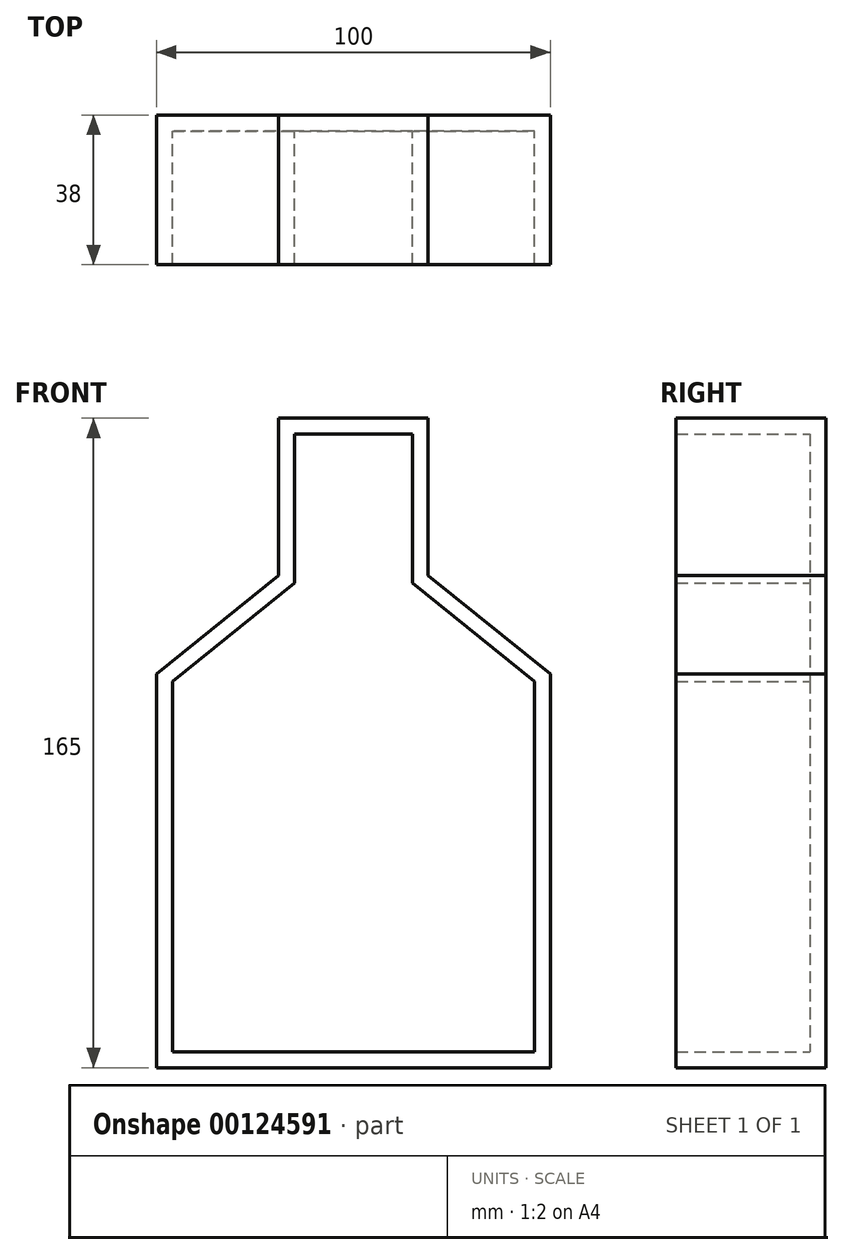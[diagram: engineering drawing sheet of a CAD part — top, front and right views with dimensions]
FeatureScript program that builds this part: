
annotation { "Feature Type Name" : "Feature", "Feature Type Description" : "" }
export const myFeature = defineFeature(function(context is Context, id is Id, definition is map)
    precondition{}
    {
        {
            var Q0;
            Q0=qCreatedBy(makeId("Front.planeOp"),FACE);
            var sketch = newSketch(context, id + "F0", { "sketchPlane" : qUnion([Q0])});
            skLineSegment(sketch, "E0", {"start": v(-50, -75) * mm, "end": v(50, -75) * mm});
            skLineSegment(sketch, "E1", {"start": v(50, -75) * mm, "end": v(50, 25) * mm});
            skLineSegment(sketch, "E2", {"start": v(19, 90) * mm, "end": v(-19, 90) * mm});
            skLineSegment(sketch, "E3", {"start": v(-50, 25) * mm, "end": v(-50, -75) * mm});
            skLineSegment(sketch, "E4", {"start": v(-19, 90) * mm, "end": v(-19, 50) * mm});
            skLineSegment(sketch, "E5", {"start": v(-19, 50) * mm, "end": v(-50, 25) * mm});
            skLineSegment(sketch, "E6", {"start": v(19, 90) * mm, "end": v(19, 50) * mm});
            skLineSegment(sketch, "E7", {"start": v(50, 25) * mm, "end": v(19, 50) * mm});
            skSolve(sketch);
        }
        {
            var Q0;
            Q0 = qSketchRegion(id + "F0", true);
            extrude(context, id + "F1", {"entities" : qUnion([Q0]), "endBound" : BoundingType.SYMMETRIC, "depth" : 38 * mm});
        }
        {
            var Q0;
            Q0=makeQuery(id+"F1.opExtrude","CAP_FACE",FACE,{"disambiguationData":[OSD([sQuery(id+"F0.wireOp",EDGE,"E0"),sQuery(id+"F0.wireOp",EDGE,"E1"),sQuery(id+"F0.wireOp",EDGE,"wSn0D2Qj-3Zax-uCmw-o4nf-oXh15RCH9NpI"),sQuery(id+"F0.wireOp",EDGE,"lb0Cxtu6-hfBw-rpJw-cRh2-uOisXKPZe3ND"),sQuery(id+"F0.wireOp",EDGE,"E2"),sQuery(id+"F0.wireOp",EDGE,"AijqVBmo-7KvU-JayF-ZtCp-XIphwKbNqpgS"),sQuery(id+"F0.wireOp",EDGE,"qnxWOC0h-Q1Qe-CmUV-2mwX-mDCYA3CNavIx"),sQuery(id+"F0.wireOp",EDGE,"E3")])],"isStart":false});
            var Q1;
            Q1=makeQuery(id+"F1.opExtrude","SWEPT_BODY",BODY,{"disambiguationData":[OSD([sQuery(id+"F0.wireOp",EDGE,"E0"),sQuery(id+"F0.wireOp",EDGE,"E1"),sQuery(id+"F0.wireOp",EDGE,"wSn0D2Qj-3Zax-uCmw-o4nf-oXh15RCH9NpI"),sQuery(id+"F0.wireOp",EDGE,"lb0Cxtu6-hfBw-rpJw-cRh2-uOisXKPZe3ND"),sQuery(id+"F0.wireOp",EDGE,"E2"),sQuery(id+"F0.wireOp",EDGE,"AijqVBmo-7KvU-JayF-ZtCp-XIphwKbNqpgS"),sQuery(id+"F0.wireOp",EDGE,"qnxWOC0h-Q1Qe-CmUV-2mwX-mDCYA3CNavIx"),sQuery(id+"F0.wireOp",EDGE,"E3")])]});
            shell(context, id + "F2", {"entities" : qUnion([Q0]), "parts" : qUnion([Q1]), "thickness" : 4 * mm});
        }
    });
